# Revit family: Mirror-Solid_Surface_Frame-Whitehall-WH1860_Series
name_source: partatom
category: Specialty Equipment
units: mm (PartAtom-declared; Revit-internal decimal feet)

## family parameters
Cut with Voids When Loaded = No
Host = Face
OmniClass Number = 23.40.95.17.17
OmniClass Title = Mirrors
Part Type = Normal
Room Calculation Point = No
Round Connector Dimension = Use Diameter
Shared = Yes

## types (5) — shared parameters
ADA Compliant = Yes
Assembly Code = E2010
Default Elevation = 40"
Description = BestCare® Ligature-Resistant Solid Surface Frame Mirror with Concealed Front Mounting
Finish = Corterra Polymer Resin-Whitehall-OCC11 Blanco White
Installation Type = Wall Mounted
Length = 3/4"
Manufacturer = Whitehall Manufacturing.
Material = Corterra Polymer Resin-Whitehall-OCC11 Blanco White
Product Documentation Link = https://www.whitehallmfg.com
Product Page URL = https://www.whitehallmfg.com
Radius = 2"
URL = https://www.whitehallmfg.com

## per-type parameters (varying)
| type | Height | Width |
| WH1860 | 17 1/2" | 14 1/2" |
| WH1861 | 27 1/2" | 17 1/2" |
| WH1862 | 25 1/2" | 19 1/2" |
| WH1863 | 38 1/2" | 21 1/2" |
| WH1864 | 38 1/2" | 28 1/2" |

note: column(s) folded — value = type name in every type: Model

## geometry (parser evidence)
native form markers: Sweep x3
no freeform markers — native parametric forms only
